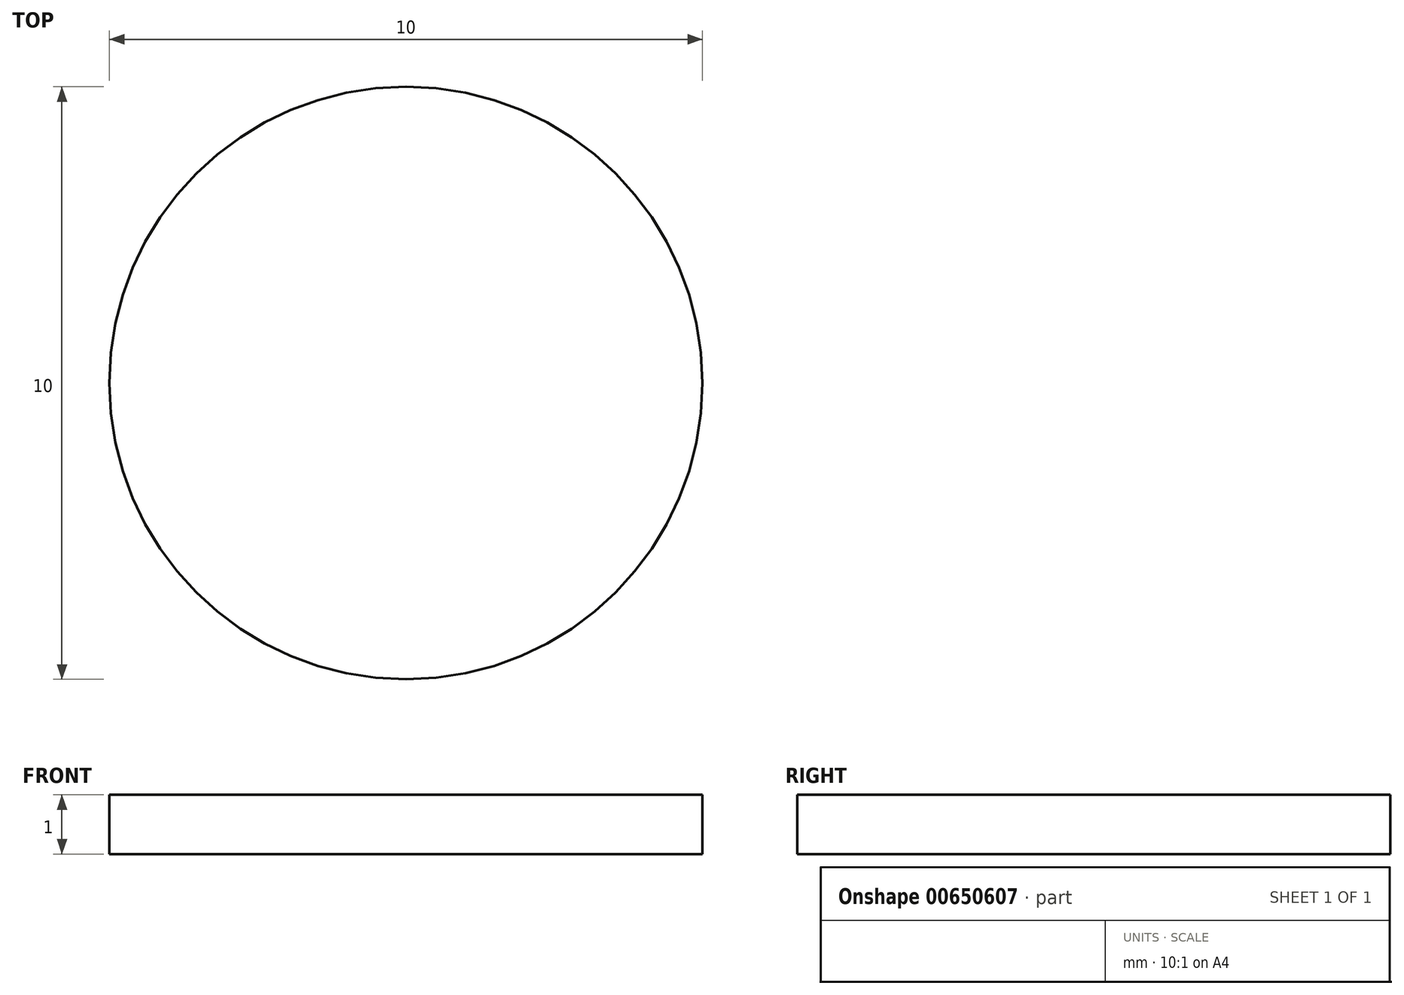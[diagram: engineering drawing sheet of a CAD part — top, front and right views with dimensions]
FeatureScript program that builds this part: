
annotation { "Feature Type Name" : "Feature", "Feature Type Description" : "" }
export const myFeature = defineFeature(function(context is Context, id is Id, definition is map)
    precondition{}
    {
        {
            var Q0;
            Q0=qCreatedBy(makeId("Top.planeOp"),FACE);
            var sketch = newSketch(context, id + "F0", { "sketchPlane" : qUnion([Q0])});
            skCircle(sketch, "E0", {"center": v(0, 0) * mm, "radius": 5 * mm});
            skSolve(sketch);
        }
        {
            var Q0;
            Q0 = qSketchRegion(id + "F0", true);
            extrude(context, id + "F1", {"entities" : qUnion([Q0]), "depth" : 6 * mm, "offsetDistance" : 25 * mm, "hasSecondDirection" : true, "secondDirectionOppositeDirection" : false, "secondDirectionDepth" : 5 * mm});
        }
    });
